# Revit family: Legrand-Enveloppes_industrielles-Metal-Armoires_Altis-P600
name_source: partatom
category: Equipement électrique
units: mm (PartAtom-declared; Revit-internal decimal feet)

## family parameters
Basée sur le plan de construction = Non
Configuration du panneau = Deux colonnes, circuits au sein
Cote de connecteur circulaire = Utiliser le diamètre
Couper avec des vides une fois chargée = Non
Numéro OmniClass = 23.80.30.11.17
Partagée = Non
Point de calcul de pièce = Non
Titre OmniClass = Distribution Boards and Control Panels
Toujours verticalement = Oui
Type d'élément = Tableau de raccordement

## types (16) — shared parameters
Conditions Générale d'Utilisation = https://export.legrand.com
ETIM Class 6.0 = EC000261
Fabricant = Legrand
IK = 10
IP = 55
Image du type = Altis_047101_pw_133028_pz_48.jpg
Matière = Polyester
RAL = 7035
URL = www.legrand.fr
aucun socle = Oui
erreur double hauteur de socle = Non
profondeur = 600 mm
socle 100mm = Non
socle 200mm = Non
socle hauteur 100 largeur 1000 = Non
socle hauteur 100 largeur 1200 = Non
socle hauteur 100 largeur 1600 = Non
socle hauteur 100 largeur 400 = Non
socle hauteur 100 largeur 600 = Non
socle hauteur 100 largeur 800 = Non
socle hauteur 200 largeur 1000 = Non
socle hauteur 200 largeur 1200 = Non
socle hauteur 200 largeur 1600 = Non
socle hauteur 200 largeur 400 = Non
socle hauteur 200 largeur 600 = Non
socle hauteur 200 largeur 800 = Non
zero-valued in all types: Elévation par défaut, hauteur socles

## per-type parameters (varying)
| type | Armoire 047240 | Armoire 047241 | Armoire 047244 | Armoire 047245 | Armoire 047246 | Armoire 047247 | Armoire 047248 | Armoire 047249 | Armoire 047250 | Armoire 047251 | Armoire 047252 | Armoire 047253 | Armoire 047254 | Armoire 047255 | Armoire 047256 | Armoire 047257 | Description | Hauteur | Largeur | Poids | distance avant zone d'installation | largeur zone d'installation | profondeur zone d'installation |
| Enveloppe industrielle - Altis - Assemblable - Métal - Profondeur 600mm - Hauteur 1200mm - Largeur  600mm | Oui | Non | Non | Non | Non | Non | Non | Non | Non | Non | Non | Non | Non | Non | Non | Non | Ref 047240 - Enveloppe industrielle - Altis - Assemblable - Métal - Profondeur 600mm | 1223 mm  [stored 4.01247 ft] | 600 mm | 67.60 kg | 600 mm | 2200 mm | 1200 mm |
| Enveloppe industrielle - Altis - Assemblable - Métal - Profondeur 600mm - Hauteur 1200mm - Largeur  800mm | Non | Oui | Non | Non | Non | Non | Non | Non | Non | Non | Non | Non | Non | Non | Non | Non | Ref 047241 - Enveloppe industrielle - Altis - Assemblable - Métal - Profondeur 600mm | 1223 mm  [stored 4.01247 ft] | 800 mm  [stored 2.62467 ft] | 83.00 kg | 800 mm  [stored 2.62467 ft] | 2400 mm | 1400 mm  [stored 4.59318 ft] |
| Enveloppe industrielle - Altis - Assemblable - Métal - Profondeur 600mm - Hauteur 1800mm - Largeur 400mm | Non | Non | Non | Non | Oui | Non | Non | Non | Non | Non | Non | Non | Non | Non | Non | Non | Ref 047246 - Enveloppe industrielle - Altis - Assemblable - Métal - Profondeur 600mm | 1823 mm  [stored 5.98097 ft] | 400 mm  [stored 1.31234 ft] | 104.00 kg | 400 mm  [stored 1.31234 ft] | 2000 mm  [stored 6.56168 ft] | 1000 mm  [stored 3.28084 ft] |
| Enveloppe industrielle - Altis - Assemblable - Métal - Profondeur 600mm - Hauteur 1600mm - Largeur  600mm | Non | Non | Non | Non | Non | Oui | Non | Non | Non | Non | Non | Non | Non | Non | Non | Non | Ref 047247 - Enveloppe industrielle - Altis - Assemblable - Métal - Profondeur 600mm | 1823 mm  [stored 5.98097 ft] | 600 mm | 79.30 kg | 600 mm | 2200 mm | 1200 mm |
| Enveloppe industrielle - Altis - Assemblable - Métal - Profondeur 600mm - Hauteur 1800mm - Largeur 800mm | Non | Non | Non | Non | Non | Non | Oui | Non | Non | Non | Non | Non | Non | Non | Non | Non | Ref 047248 - Enveloppe industrielle - Altis - Assemblable - Métal - Profondeur 600mm | 1823 mm  [stored 5.98097 ft] | 800 mm  [stored 2.62467 ft] | 93.10 kg | 800 mm  [stored 2.62467 ft] | 2400 mm | 1400 mm  [stored 4.59318 ft] |
| Enveloppe industrielle - Altis - Assemblable - Métal - Profondeur 600mm - Hauteur 1800mm - Largeur 1000mm - Avec recentrage porte | Non | Non | Non | Non | Non | Non | Non | Oui | Non | Non | Non | Non | Non | Non | Non | Non | Ref 047249 - Enveloppe industrielle - Altis - Assemblable - Métal - Profondeur 600mm | 1823 mm  [stored 5.98097 ft] | 1000 mm  [stored 3.28084 ft] | 106.40 kg | 1000 mm  [stored 3.28084 ft] | 2600 mm  [stored 8.53018 ft] | 1600 mm  [stored 5.24934 ft] |
| Enveloppe industrielle - Altis - Assemblable - Métal - Profondeur 600mm - Hauteur 1800mm - Largeur 1200mm | Non | Non | Non | Non | Non | Non | Non | Non | Oui | Non | Non | Non | Non | Non | Non | Non | Ref 047250 - Enveloppe industrielle - Altis - Assemblable - Métal - Profondeur 600mm | 1823 mm  [stored 5.98097 ft] | 1200 mm | 137.40 kg | 1200 mm | 2800 mm  [stored 9.18635 ft] | 1800 mm  [stored 5.90551 ft] |
| Enveloppe industrielle - Altis - Assemblable - Métal - Profondeur 600mm - Hauteur 2000mm - Largeur  400mm | Non | Non | Non | Non | Non | Non | Non | Non | Non | Oui | Non | Non | Non | Non | Non | Non | Ref 047251 - Enveloppe industrielle - Altis - Assemblable - Métal - Profondeur 600mm | 2023 mm  [stored 6.63714 ft] | 400 mm  [stored 1.31234 ft] | 60.10 kg | 400 mm  [stored 1.31234 ft] | 2000 mm  [stored 6.56168 ft] | 1000 mm  [stored 3.28084 ft] |
| Enveloppe industrielle - Altis - Assemblable - Métal - Profondeur 600mm - Hauteur 2000mm - Largeur  600mm | Non | Non | Non | Non | Non | Non | Non | Non | Non | Non | Oui | Non | Non | Non | Non | Non | Ref 047252 - Enveloppe industrielle - Altis - Assemblable - Métal - Profondeur 600mm | 2023 mm  [stored 6.63714 ft] | 600 mm | 83.20 kg | 600 mm | 2200 mm | 1200 mm |
| Enveloppe industrielle - Altis - Assemblable - Métal - Profondeur 600mm - Hauteur 2000mm - Largeur  800mm | Non | Non | Non | Non | Non | Non | Non | Non | Non | Non | Non | Oui | Non | Non | Non | Non | Ref 047253 - Enveloppe industrielle - Altis - Assemblable - Métal - Profondeur 600mm | 2023 mm  [stored 6.63714 ft] | 800 mm  [stored 2.62467 ft] | 98.00 kg | 800 mm  [stored 2.62467 ft] | 2400 mm | 1400 mm  [stored 4.59318 ft] |
| Enveloppe industrielle - Altis - Assemblable - Métal - Profondeur 600mm - Hauteur 2000mm - Largeur 1000mm - Avec recentrage porte | Non | Non | Non | Non | Non | Non | Non | Non | Non | Non | Non | Non | Oui | Non | Non | Non | Ref 047254 - Enveloppe industrielle - Altis - Assemblable - Métal - Profondeur 600mm | 2023 mm  [stored 6.63714 ft] | 1000 mm  [stored 3.28084 ft] | 112.30 kg | 1000 mm  [stored 3.28084 ft] | 2600 mm  [stored 8.53018 ft] | 1600 mm  [stored 5.24934 ft] |
| Enveloppe industrielle - Altis - Assemblable - Métal - Profondeur 600mm - Hauteur 2000mm - Largeur  1000mm | Non | Non | Non | Non | Non | Non | Non | Non | Non | Non | Non | Non | Non | Oui | Non | Non | Ref 047255 - Enveloppe industrielle - Altis - Assemblable - Métal - Profondeur 600mm | 2023 mm  [stored 6.63714 ft] | 1000 mm  [stored 3.28084 ft] | 117.00 kg | 1000 mm  [stored 3.28084 ft] | 2600 mm  [stored 8.53018 ft] | 1600 mm  [stored 5.24934 ft] |
| Enveloppe industrielle - Altis - Assemblable - Métal - Profondeur 600mm - Hauteur 2000mm - Largeur  1200mm | Non | Non | Non | Non | Non | Non | Non | Non | Non | Non | Non | Non | Non | Non | Oui | Non | Ref 047256 - Enveloppe industrielle - Altis - Assemblable - Métal - Profondeur 600mm | 2023 mm  [stored 6.63714 ft] | 1200 mm | 144.30 kg | 1200 mm | 2800 mm  [stored 9.18635 ft] | 1800 mm  [stored 5.90551 ft] |
| Enveloppe industrielle - Altis - Assemblable - Métal - Profondeur 600mm - Hauteur 2000mm - Largeur  1600mm | Non | Non | Non | Non | Non | Non | Non | Non | Non | Non | Non | Non | Non | Non | Non | Oui | Ref 047257 - Enveloppe industrielle - Altis - Assemblable - Métal - Profondeur 600mm | 2023 mm  [stored 6.63714 ft] | 1600 mm  [stored 5.24934 ft] | 150.50 kg | 1600 mm  [stored 5.24934 ft] | 3200 mm  [stored 10.4987 ft] | 2200 mm |
| Enveloppe industrielle - Altis - Assemblable - Métal - Profondeur 600mm - Hauteur 1800mm - Largeur 600mm | Non | Non | Oui | Non | Non | Non | Non | Non | Non | Non | Non | Non | Non | Non | Non | Non | Ref 047244 - Enveloppe industrielle - Altis - Assemblable - Métal - Profondeur 600mm | 1623 mm  [stored 5.3248 ft] | 600 mm | 148.00 kg | 600 mm | 2200 mm | 1200 mm |
| Enveloppe industrielle - Altis - Assemblable - Métal - Profondeur 600mm - Hauteur 1600mm - Largeur  800mm | Non | Non | Non | Oui | Non | Non | Non | Non | Non | Non | Non | Non | Non | Non | Non | Non | Ref 047245 - Enveloppe industrielle - Altis - Assemblable - Métal - Profondeur 600mm | 1623 mm  [stored 5.3248 ft] | 800 mm  [stored 2.62467 ft] | 88.20 kg | 800 mm  [stored 2.62467 ft] | 2400 mm | 1400 mm  [stored 4.59318 ft] |

note: [stored X ft] marks values corroborated as IEEE doubles in the binary element streams (Revit-internal decimal feet)
